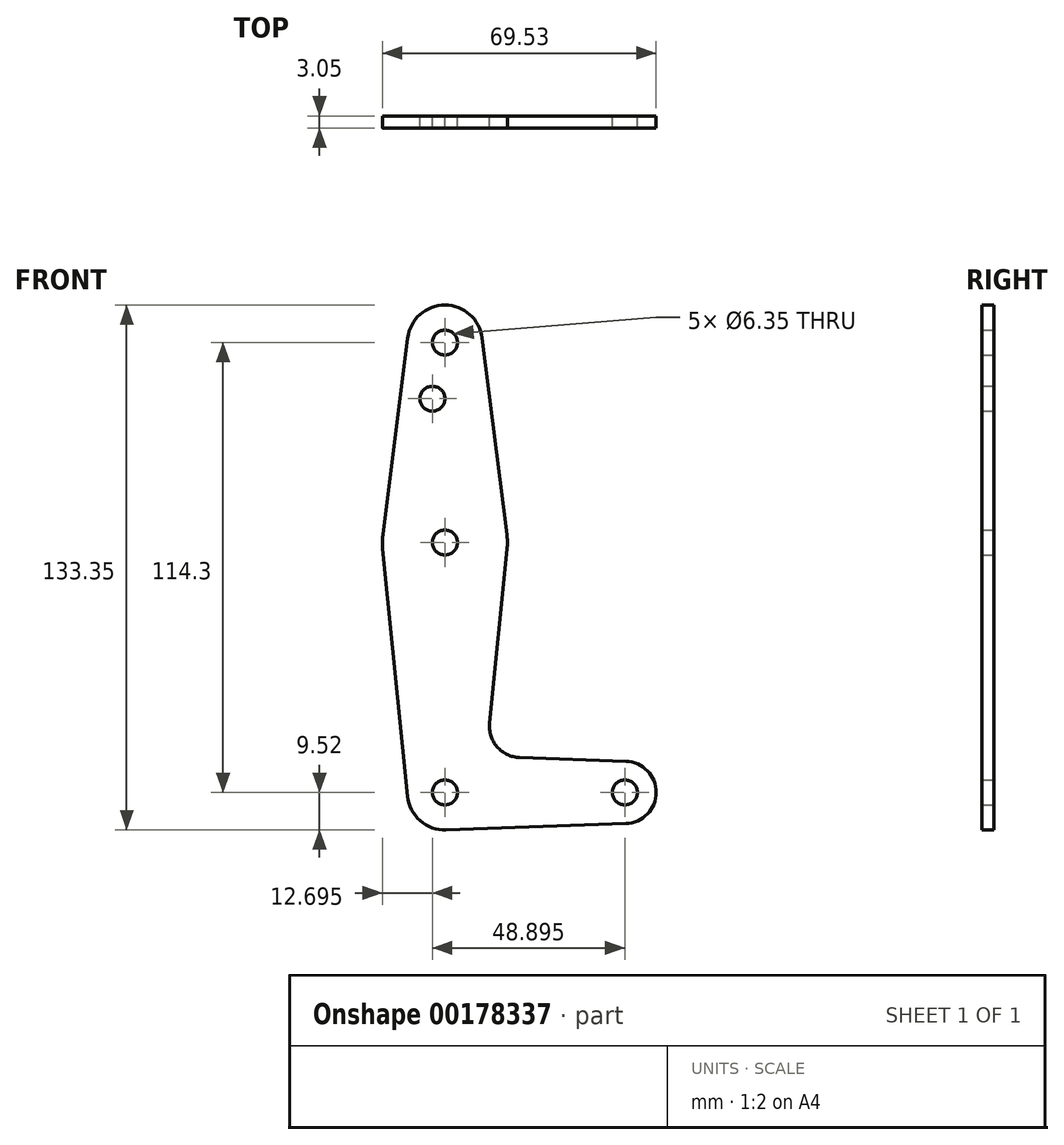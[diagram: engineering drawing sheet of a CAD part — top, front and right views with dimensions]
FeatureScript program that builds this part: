
annotation { "Feature Type Name" : "Feature", "Feature Type Description" : "" }
export const myFeature = defineFeature(function(context is Context, id is Id, definition is map)
    precondition{}
    {
        {
            var Q0;
            Q0=qCreatedBy(makeId("Front.planeOp"),FACE);
            var sketch = newSketch(context, id + "F0", { "sketchPlane" : qUnion([Q0])});
            skLineSegment(sketch, "E0", {"start": v(0, 114.3) * mm, "end": v(0, 0) * mm, "construction": true});
            skLineSegment(sketch, "E1", {"start": v(0, 0) * mm, "end": v(45.72, 0) * mm, "construction": true});
            skCircle(sketch, "E2", {"center": v(0, 114.3) * mm, "radius": 9.53 * mm});
            skCircle(sketch, "E3", {"center": v(0, 63.5) * mm, "radius": 15.88 * mm});
            skCircle(sketch, "E4", {"center": v(0, 0) * mm, "radius": 9.53 * mm});
            skCircle(sketch, "E5", {"center": v(45.72, 0) * mm, "radius": 7.94 * mm});
            skLineSegment(sketch, "E6", {"start": v(-9.45, 115.5) * mm, "end": v(-15.75, 65.48) * mm});
            skLineSegment(sketch, "E7", {"start": v(-15.8, 61.91) * mm, "end": v(-9.48, -0.95) * mm});
            skLineSegment(sketch, "E8.MirrorCS", {"start": v(9.45, 115.5) * mm, "end": v(15.75, 65.48) * mm});
            skLineSegment(sketch, "E9.MirrorCS", {"start": v(15.8, 61.91) * mm, "end": v(11.34, 17.61) * mm});
            skLineSegment(sketch, "E10", {"start": v(46, 7.93) * mm, "end": v(18.98, 8.87) * mm});
            skLineSegment(sketch, "E11", {"start": v(0.33, -9.52) * mm, "end": v(46, -7.93) * mm});
            skCircle(sketch, "E12", {"center": v(0, 114.3) * mm, "radius": 3.18 * mm});
            skCircle(sketch, "E13", {"center": v(0, 63.5) * mm, "radius": 3.18 * mm});
            skCircle(sketch, "E14", {"center": v(0, 0) * mm, "radius": 3.18 * mm});
            skCircle(sketch, "E15", {"center": v(45.72, 0) * mm, "radius": 3.18 * mm});
            skCircle(sketch, "E16", {"center": v(-3.18, 100.03) * mm, "radius": 3.18 * mm});
            skPoint(sketch, "E17.newPointA", {"position": v(9.48, -0.95) * mm});
            skArc(sketch, "E17.filletArc", {"start": v(11.34, 17.61) * mm, "mid": v(13.27, 11.59) * mm, "end": v(18.98, 8.87) * mm});
            skSolve(sketch);
        }
        {
            var Q0;
            Q0=makeQuery(id+"F0.imprint","IMPRINT",FACE,{"disambiguationData":[TD([[makeQuery(id+"F0.imprint","IMPRINT",EDGE,{"derivedFrom":sQuery(id+"F0.wireOp",EDGE,"E12")}),-1.0]])]});
            var Q1;
            {var subQ1=sQuery(id+"F0.wireOp",EDGE,"E6");Q1=makeQuery(id+"F0.imprint","IMPRINT",FACE,{"disambiguationData":[TD([[makeQuery(id+"F0.imprint","IMPRINT",EDGE,{"derivedFrom":subQ1}),1.0]])]});}
            var Q2;
            Q2=makeQuery(id+"F0.imprint","IMPRINT",FACE,{"disambiguationData":[TD([[makeQuery(id+"F0.imprint","IMPRINT",EDGE,{"derivedFrom":sQuery(id+"F0.wireOp",EDGE,"E13")}),-1.0]])]});
            var Q3;
            {var subQ0=sQuery(id+"F0.wireOp",EDGE,"E7");Q3=makeQuery(id+"F0.imprint","IMPRINT",FACE,{"disambiguationData":[TD([[makeQuery(id+"F0.imprint","IMPRINT",EDGE,{"derivedFrom":subQ0}),1.0]])]});}
            var Q4;
            Q4=makeQuery(id+"F0.imprint","IMPRINT",FACE,{"disambiguationData":[TD([[makeQuery(id+"F0.imprint","IMPRINT",EDGE,{"derivedFrom":sQuery(id+"F0.wireOp",EDGE,"E14")}),-1.0]])]});
            var Q5;
            Q5=makeQuery(id+"F0.imprint","IMPRINT",FACE,{"disambiguationData":[TD([[makeQuery(id+"F0.imprint","IMPRINT",EDGE,{"derivedFrom":sQuery(id+"F0.wireOp",EDGE,"E15")}),-1.0]])]});
            extrude(context, id + "F1", {"entities" : qUnion([Q0, Q1, Q2, Q3, Q4, Q5]), "depth" : 3.05 * mm});
        }
    });
